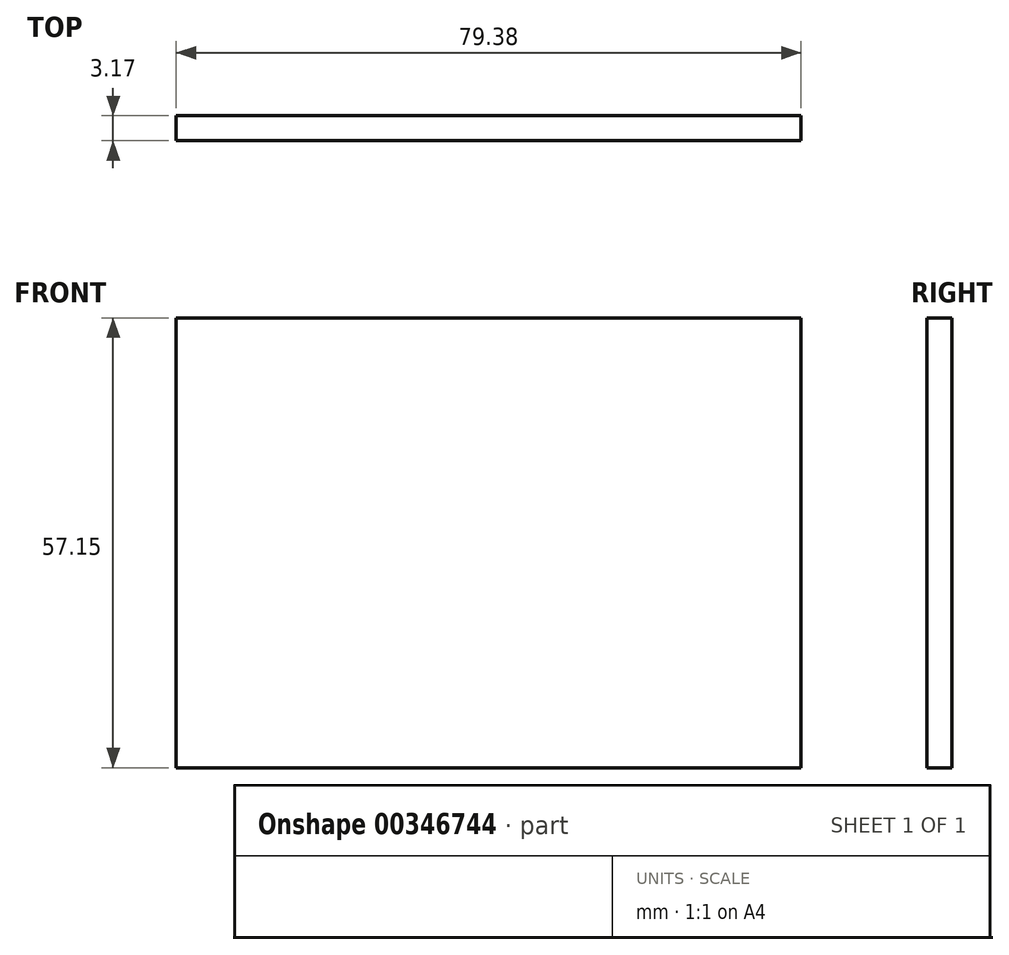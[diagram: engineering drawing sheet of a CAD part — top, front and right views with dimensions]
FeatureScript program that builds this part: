
annotation { "Feature Type Name" : "Feature", "Feature Type Description" : "" }
export const myFeature = defineFeature(function(context is Context, id is Id, definition is map)
    precondition{}
    {
        {
            var Q0;
            Q0=qCreatedBy(makeId("Front.planeOp"),FACE);
            var sketch = newSketch(context, id + "F0", { "sketchPlane" : qUnion([Q0])});
            skLineSegment(sketch, "E0.bottom", {"start": v(-39.69, -26.99) * mm, "end": v(-39.69, 30.16) * mm});
            skLineSegment(sketch, "E0.top", {"start": v(39.69, -26.99) * mm, "end": v(39.69, 30.16) * mm});
            skLineSegment(sketch, "E0.left", {"start": v(-39.69, -26.99) * mm, "end": v(39.69, -26.99) * mm});
            skLineSegment(sketch, "E0.right", {"start": v(-39.69, 30.16) * mm, "end": v(39.69, 30.16) * mm});
            skSolve(sketch);
        }
        {
            var Q0;
            Q0=makeQuery(id+"F0.imprint","IMPRINT",FACE,{"disambiguationData":[TD([[makeQuery(id+"F0.imprint","IMPRINT",EDGE,{"derivedFrom":sQuery(id+"F0.wireOp",EDGE,"E0.bottom")}),-1.0]])]});
            extrude(context, id + "F1", {"entities" : qUnion([Q0]), "oppositeDirection" : true, "depth" : 3.17 * mm});
        }
    });
